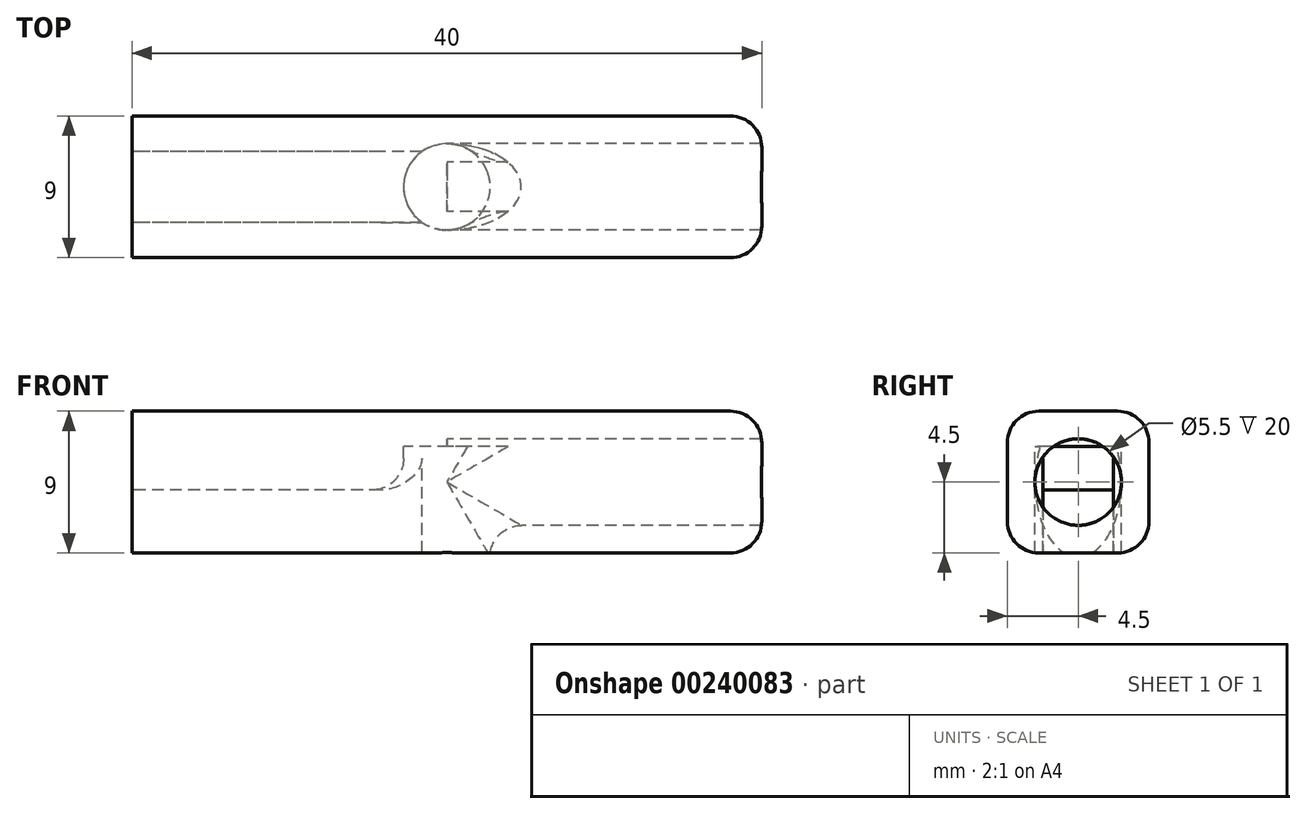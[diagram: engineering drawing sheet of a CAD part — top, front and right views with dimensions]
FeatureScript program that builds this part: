
annotation { "Feature Type Name" : "Feature", "Feature Type Description" : "" }
export const myFeature = defineFeature(function(context is Context, id is Id, definition is map)
    precondition{}
    {
        {
            var Q0;
            Q0=qCreatedBy(makeId("Top.planeOp"),FACE);
            var sketch = newSketch(context, id + "F0", { "sketchPlane" : qUnion([Q0])});
            skLineSegment(sketch, "E0.bottom", {"start": v(-20, 4.5) * mm, "end": v(18, 4.5) * mm});
            skLineSegment(sketch, "E0.top", {"start": v(-20, -4.5) * mm, "end": v(18, -4.5) * mm});
            skLineSegment(sketch, "E0.left", {"start": v(-20, 4.5) * mm, "end": v(-20, -4.5) * mm});
            skLineSegment(sketch, "E0.right", {"start": v(20, 2.5) * mm, "end": v(20, -2.5) * mm});
            skPoint(sketch, "E0.middle", {"position": v(0, 0) * mm});
            skPoint(sketch, "E1.visualSharp", {"position": v(20, 4.5) * mm});
            skArc(sketch, "E1.filletArc", {"start": v(20, 2.5) * mm, "mid": v(19.41, 3.91) * mm, "end": v(18, 4.5) * mm});
            skPoint(sketch, "E2.visualSharp", {"position": v(20, -4.5) * mm});
            skArc(sketch, "E2.filletArc", {"start": v(18, -4.5) * mm, "mid": v(19.41, -3.91) * mm, "end": v(20, -2.5) * mm});
            skSolve(sketch);
        }
        {
            var Q0;
            Q0=makeQuery(id+"F0.imprint","IMPRINT",FACE,{"disambiguationData":[TD([[makeQuery(id+"F0.imprint","IMPRINT",EDGE,{"derivedFrom":sQuery(id+"F0.wireOp",EDGE,"E0.bottom")}),-1.0]])]});
            extrude(context, id + "F1", {"entities" : qUnion([Q0]), "depth" : 4.5 * mm, "hasSecondDirection" : true, "secondDirectionOppositeDirection" : true, "secondDirectionDepth" : 4.5 * mm});
        }
        {
            var Q0;
            Q0=makeQuery(id+"F1.opExtrude","CAP_EDGE",EDGE,{"disambiguationData":[OSD([sQuery(id+"F0.wireOp",EDGE,"E0.bottom")])],"isStart":false});
            var Q1;
            Q1=makeQuery(id+"F1.opExtrude","CAP_EDGE",EDGE,{"disambiguationData":[OSD([sQuery(id+"F0.wireOp",EDGE,"E0.bottom")])],"isStart":true});
            var Q2;
            Q2=makeQuery(id+"F1.opExtrude","CAP_EDGE",EDGE,{"disambiguationData":[OSD([sQuery(id+"F0.wireOp",EDGE,"E0.top")])],"isStart":true});
            var Q3;
            Q3=makeQuery(id+"F1.opExtrude","CAP_EDGE",EDGE,{"disambiguationData":[OSD([sQuery(id+"F0.wireOp",EDGE,"E0.top")])],"isStart":false});
            var Q4;
            Q4=makeQuery(id+"F1.opExtrude","CAP_EDGE",EDGE,{"disambiguationData":[OSD([sQuery(id+"F0.wireOp",EDGE,"E0.right")])],"isStart":true});
            var Q5;
            Q5=makeQuery(id+"F1.opExtrude","CAP_EDGE",EDGE,{"disambiguationData":[OSD([sQuery(id+"F0.wireOp",EDGE,"E0.right")])],"isStart":false});
            fillet(context, id + "F2", {"entities" : qUnion([Q0, Q1, Q2, Q3, Q4, Q5]), "radius" : 2 * mm, "allowEdgeOverflow" : false});
        }
        {
            var Q0;
            Q0=qCreatedBy(makeId("Top.planeOp"),FACE);
            cPlane(context, id + "F3", {"entities" : qUnion([Q0]), "cplaneType" : CPlaneType.OFFSET, "offset" : 2.25 * mm, "width" : 150 * mm, "height" : 150 * mm});
        }
        {
            var Q0;
            Q0=qCreatedBy(id+"F3.planeOp",FACE);
            var sketch = newSketch(context, id + "F4", { "sketchPlane" : qUnion([Q0])});
            skCircle(sketch, "E3", {"center": v(0, 0) * mm, "radius": 2.75 * mm});
            skSolve(sketch);
        }
        {
            var Q0;
            Q0 = qSketchRegion(id + "F4", true);
            extrude(context, id + "F5", {"entities" : qUnion([Q0]), "operationType" : NewBodyOperationType.REMOVE, "oppositeDirection" : true, "depth" : 9 * mm});
        }
        {
            var Q0;
            Q0=qCreatedBy(makeId("Right.planeOp"),FACE);
            var sketch = newSketch(context, id + "F6", { "sketchPlane" : qUnion([Q0])});
            skCircle(sketch, "E4", {"center": v(0, 0) * mm, "radius": 2.75 * mm});
            skSolve(sketch);
        }
        {
            var Q0;
            Q0=makeQuery(id+"F6.imprint","IMPRINT",FACE,{"disambiguationData":[TD([[makeQuery(id+"F6.imprint","IMPRINT",EDGE,{"derivedFrom":sQuery(id+"F6.wireOp",EDGE,"E4")}),1.0]])]});
            var Q1;
            Q1=sQuery(id+"F6.wireOp",EDGE,"E4");
            extrude(context, id + "F7", {"entities" : qUnion([Q0]), "operationType" : NewBodyOperationType.REMOVE, "surfaceEntities" : qUnion([Q1]), "endBound" : BoundingType.THROUGH_ALL, "offsetDistance" : 25 * mm, "depth" : 30 * mm});
        }
        {
            var Q0;
            {var subQ0=sQuery(id+"F0.wireOp",EDGE,"E0.left");var subQ1=sQuery(id+"F0.wireOp",EDGE,"E0.bottom");var subQ2=sQuery(id+"F0.wireOp",EDGE,"E0.top");Q0=makeQuery(id+"F5.boolean.opBoolean","SPLIT",FACE,{"disambiguationData":[TD([makeQuery(id+"F1.opExtrude","SWEPT_FACE",FACE,{"disambiguationData":[OSD([subQ0])]})])],"derivedFrom":makeQuery(id+"F1.opExtrude","CAP_FACE",FACE,{"disambiguationData":[OSD([subQ1,subQ2,subQ0,sQuery(id+"F0.wireOp",EDGE,"E0.right"),sQuery(id+"F0.wireOp",EDGE,"E1.filletArc"),sQuery(id+"F0.wireOp",EDGE,"E2.filletArc")])],"isStart":true})});}
            var sketch = newSketch(context, id + "F8", { "sketchPlane" : qUnion([Q0])});
            skLineSegment(sketch, "E5", {"start": v(0, 0) * mm, "end": v(-20, 0) * mm, "construction": true});
            skLineSegment(sketch, "E6.bottom", {"start": v(0, -2.25) * mm, "end": v(-20, -2.25) * mm});
            skLineSegment(sketch, "E6.top", {"start": v(0, 2.25) * mm, "end": v(-20, 2.25) * mm});
            skLineSegment(sketch, "E6.left", {"start": v(0, -2.25) * mm, "end": v(0, 2.25) * mm});
            skLineSegment(sketch, "E6.right", {"start": v(-20, -2.25) * mm, "end": v(-20, 2.25) * mm});
            skPoint(sketch, "E6.middle", {"position": v(-10, 0) * mm});
            skSolve(sketch);
        }
        {
            var Q0;
            Q0 = qSketchRegion(id + "F8", true);
            extrude(context, id + "F9", {"entities" : qUnion([Q0]), "operationType" : NewBodyOperationType.REMOVE, "oppositeDirection" : true, "offsetDistance" : 25 * mm, "depth" : 4 * mm});
        }
        {
            var Q0;
            Q0=makeQuery(id+"F7.boolean.opBoolean","INTERSECT",EDGE,{"derivedFrom":[makeQuery(id+"F5.boolean.opBoolean","COPY",FACE,{"derivedFrom":makeQuery(id+"F5.opExtrude","SWEPT_FACE",FACE,{"disambiguationData":[OSD([sQuery(id+"F4.wireOp",EDGE,"E3")])]})}),makeQuery(id+"F7.opExtrude","SWEPT_FACE",FACE,{"disambiguationData":[OSD([sQuery(id+"F6.wireOp",EDGE,"E4")])]})]});
            var Q1;
            Q1=makeQuery(id+"F9.boolean.opBoolean","INTERSECT",EDGE,{"derivedFrom":[makeQuery(id+"F5.boolean.opBoolean","COPY",FACE,{"derivedFrom":makeQuery(id+"F5.opExtrude","SWEPT_FACE",FACE,{"disambiguationData":[OSD([sQuery(id+"F4.wireOp",EDGE,"E3")])]})}),makeQuery(id+"F9.opExtrude","CAP_FACE",FACE,{"disambiguationData":[OSD([sQuery(id+"F8.wireOp",EDGE,"E6.bottom"),sQuery(id+"F8.wireOp",EDGE,"E6.top"),sQuery(id+"F8.wireOp",EDGE,"E6.left"),sQuery(id+"F8.wireOp",EDGE,"E6.right")])],"isStart":false})]});
            fillet(context, id + "F10", {"entities" : qUnion([Q0, Q1]), "radius" : 2 * mm, "tangentPropagation" : true, "allowEdgeOverflow" : false});
        }
    });
